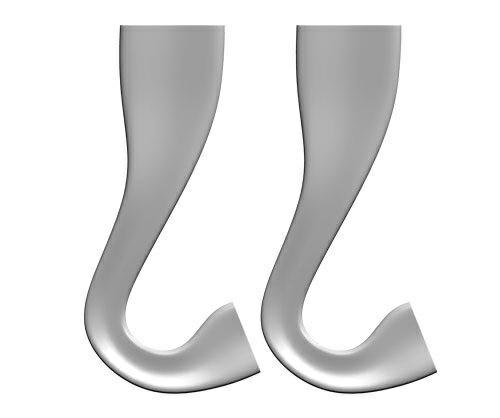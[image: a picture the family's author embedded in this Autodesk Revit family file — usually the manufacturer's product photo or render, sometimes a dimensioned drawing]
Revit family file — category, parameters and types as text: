
# Revit family: CITY ALPHABET litera „U”
name_source: partatom
category: Meble
revit_build: Autodesk Revit 2018 (Build: 20190510_1515(x64)
units: mm (PartAtom-declared; Revit-internal decimal feet)

## family parameters
Numer OmniClass = 23.40.10.11.14
Obiekt nadrzędny = Powierzchnia
Punkt obliczania pomieszczeń = Nie
Tnij formami wycięć po wczytaniu = Nie
Tytuł OmniClass = Exterior Seating
Współdzielony = Nie

## types (1)
- CITY ALPHABET litera „U”
    Domyślna rzędna = 1219 mm
    Długość = 2250 mm
    IfcExportAs = IfcFurnishingElement
    Komentarze do typu = Ławka
    Materiał - informacja = Szeroki wybór kolorów wg palety RAL. Istnieje również możliwość specjalnego wykonania
kolorystycznego na indywidualne zapytanie klienta.
    Model = CITY ALPHABET litera „U”
    Obraz typu = U.jpg
    Producent = Astrini Design
    Szerokość = 2350 mm
    Temepratura użytkowania = -40°C do 80°C, ( -40°F do 176°F )
    URL = http://astrini-design.pl
    Waga (szacunkowo) = 69.00 kg
    Waga po wypełnieniu (szacunkowo) = 169.00 kg
    Wysokość = 420 mm  [stored 1.37795 ft]

note: [stored X ft] marks values corroborated as IEEE doubles in the binary element streams (Revit-internal decimal feet)
